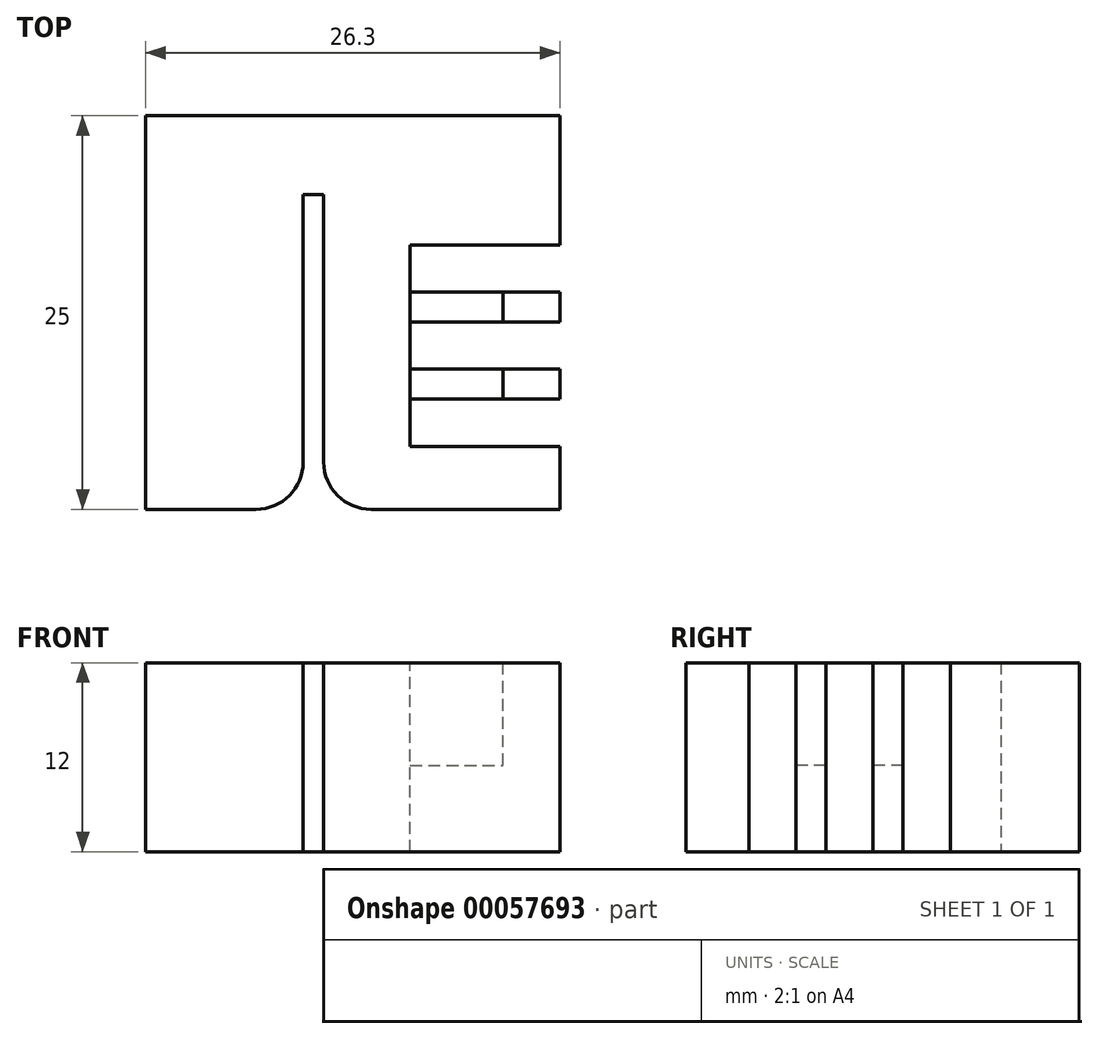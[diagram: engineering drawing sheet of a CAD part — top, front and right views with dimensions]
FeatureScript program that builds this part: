
annotation { "Feature Type Name" : "Feature", "Feature Type Description" : "" }
export const myFeature = defineFeature(function(context is Context, id is Id, definition is map)
    precondition{}
    {
        {
            var Q0;
            Q0=qCreatedBy(makeId("Top.planeOp"),FACE);
            var sketch = newSketch(context, id + "F0", { "sketchPlane" : qUnion([Q0])});
            skLineSegment(sketch, "E0.bottom", {"start": v(-11.3, 25) * mm, "end": v(15, 25) * mm});
            skLineSegment(sketch, "E0.top", {"start": v(-11.3, 0) * mm, "end": v(-1.3, 0) * mm});
            skLineSegment(sketch, "E0.left", {"start": v(-11.3, 25) * mm, "end": v(-11.3, 0) * mm});
            skLineSegment(sketch, "E0.right", {"start": v(15, 25) * mm, "end": v(15, 0) * mm});
            skLineSegment(sketch, "E1.top", {"start": v(-1.3, 20) * mm, "end": v(0, 20) * mm});
            skLineSegment(sketch, "E1.left", {"start": v(-1.3, 0) * mm, "end": v(-1.3, 20) * mm});
            skLineSegment(sketch, "E1.right", {"start": v(0, 0) * mm, "end": v(0, 20) * mm});
            skLineSegment(sketch, "E2.trimOffspring", {"start": v(0, 0) * mm, "end": v(15, 0) * mm});
            skLineSegment(sketch, "E3", {"start": v(0, 20) * mm, "end": v(0, 25) * mm});
            skSolve(sketch);
        }
        {
            var Q0;
            Q0=makeQuery(id+"F0.imprint","IMPRINT",FACE,{"disambiguationData":[TD([[makeQuery(id+"F0.imprint","IMPRINT",EDGE,{"derivedFrom":sQuery(id+"F0.wireOp",EDGE,"E0.top")}),1.0]])]});
            var Q1;
            {var subQ1=sQuery(id+"F0.wireOp",EDGE,"E0.right");Q1=makeQuery(id+"F0.imprint","IMPRINT",FACE,{"disambiguationData":[TD([[makeQuery(id+"F0.imprint","IMPRINT",EDGE,{"derivedFrom":subQ1}),-1.0]])]});}
            extrude(context, id + "F1", {"entities" : qUnion([Q0, Q1]), "depth" : 12 * mm});
        }
        {
            var Q0;
            Q0=makeQuery(id+"F1.opExtrude","CAP_FACE",FACE,{"disambiguationData":[OSD([sQuery(id+"F0.wireOp",EDGE,"E0.bottom"),sQuery(id+"F0.wireOp",EDGE,"E0.top"),sQuery(id+"F0.wireOp",EDGE,"E0.left"),sQuery(id+"F0.wireOp",EDGE,"E0.right"),sQuery(id+"F0.wireOp",EDGE,"E1.top"),sQuery(id+"F0.wireOp",EDGE,"E1.left"),sQuery(id+"F0.wireOp",EDGE,"E1.right"),sQuery(id+"F0.wireOp",EDGE,"E2.trimOffspring")])],"isStart":false});
            var sketch = newSketch(context, id + "F2", { "sketchPlane" : qUnion([Q0])});
            skLineSegment(sketch, "E4.bottom", {"start": v(5.5, 16.8) * mm, "end": v(11.4, 16.8) * mm});
            skLineSegment(sketch, "E4.top", {"start": v(5.5, 4) * mm, "end": v(11.4, 4) * mm});
            skLineSegment(sketch, "E4.left", {"start": v(5.5, 16.8) * mm, "end": v(5.5, 4) * mm});
            skLineSegment(sketch, "E4.right", {"start": v(11.4, 16.8) * mm, "end": v(11.4, 4) * mm});
            skLineSegment(sketch, "E5", {"start": v(11.4, 4) * mm, "end": v(15, 4) * mm});
            skSolve(sketch);
        }
        {
            var Q0;
            Q0=qSketchRegion(id+"F2",true);
            extrude(context, id + "F3", {"entities" : qUnion([Q0]), "operationType" : NewBodyOperationType.REMOVE, "oppositeDirection" : true, "depth" : 6.5 * mm});
        }
        {
            var Q0;
            Q0=makeQuery(id+"F1.opExtrude","CAP_FACE",FACE,{"disambiguationData":[OSD([sQuery(id+"F0.wireOp",EDGE,"E0.bottom"),sQuery(id+"F0.wireOp",EDGE,"E0.top"),sQuery(id+"F0.wireOp",EDGE,"E0.left"),sQuery(id+"F0.wireOp",EDGE,"E0.right"),sQuery(id+"F0.wireOp",EDGE,"E1.top"),sQuery(id+"F0.wireOp",EDGE,"E1.left"),sQuery(id+"F0.wireOp",EDGE,"E1.right"),sQuery(id+"F0.wireOp",EDGE,"E2.trimOffspring")])],"isStart":false});
            var sketch = newSketch(context, id + "F4", { "sketchPlane" : qUnion([Q0])});
            skLineSegment(sketch, "E6.bottom", {"start": v(5.5, 16.8) * mm, "end": v(15, 16.8) * mm});
            skLineSegment(sketch, "E6.top", {"start": v(5.5, 13.8) * mm, "end": v(15, 13.8) * mm});
            skLineSegment(sketch, "E6.left", {"start": v(5.5, 16.8) * mm, "end": v(5.5, 13.8) * mm});
            skLineSegment(sketch, "E6.right", {"start": v(15, 16.8) * mm, "end": v(15, 13.8) * mm});
            skLineSegment(sketch, "E7.bottom", {"start": v(5.5, 4) * mm, "end": v(15, 4) * mm});
            skLineSegment(sketch, "E7.top", {"start": v(5.5, 7) * mm, "end": v(15, 7) * mm});
            skLineSegment(sketch, "E7.left", {"start": v(5.5, 4) * mm, "end": v(5.5, 7) * mm});
            skLineSegment(sketch, "E7.right", {"start": v(15, 4) * mm, "end": v(15, 7) * mm});
            skLineSegment(sketch, "E8.bottom", {"start": v(5.5, 8.9) * mm, "end": v(15, 8.9) * mm});
            skLineSegment(sketch, "E8.top", {"start": v(5.5, 11.9) * mm, "end": v(15, 11.9) * mm});
            skLineSegment(sketch, "E8.left", {"start": v(5.5, 8.9) * mm, "end": v(5.5, 11.9) * mm});
            skLineSegment(sketch, "E8.right", {"start": v(15, 8.9) * mm, "end": v(15, 11.9) * mm});
            skLineSegment(sketch, "E9", {"start": v(5.5, 11.9) * mm, "end": v(5.5, 13.8) * mm});
            skLineSegment(sketch, "E10", {"start": v(5.5, 7) * mm, "end": v(5.5, 8.9) * mm});
            skSolve(sketch);
        }
        {
            var Q0;
            Q0=qSketchRegion(id+"F4",true);
            extrude(context, id + "F5", {"entities" : qUnion([Q0]), "operationType" : NewBodyOperationType.REMOVE, "endBound" : BoundingType.THROUGH_ALL, "oppositeDirection" : true, "depth" : 25 * mm});
        }
        {
            var Q0;
            Q0=makeQuery(id+"F1.opExtrude","SWEPT_EDGE",EDGE,{"disambiguationData":[OSD([sQuery(id+"F0.wireOp",EDGE,"E0.top"),sQuery(id+"F0.wireOp",EDGE,"E1.left")])]});
            var Q1;
            Q1=makeQuery(id+"F1.opExtrude","SWEPT_EDGE",EDGE,{"disambiguationData":[OSD([sQuery(id+"F0.wireOp",EDGE,"E1.right"),sQuery(id+"F0.wireOp",EDGE,"E2.trimOffspring")])]});
            fillet(context, id + "F6", {"entities" : qUnion([Q0, Q1]), "radius" : 3 * mm, "tangentPropagation" : true, "allowEdgeOverflow" : false});
        }
    });
